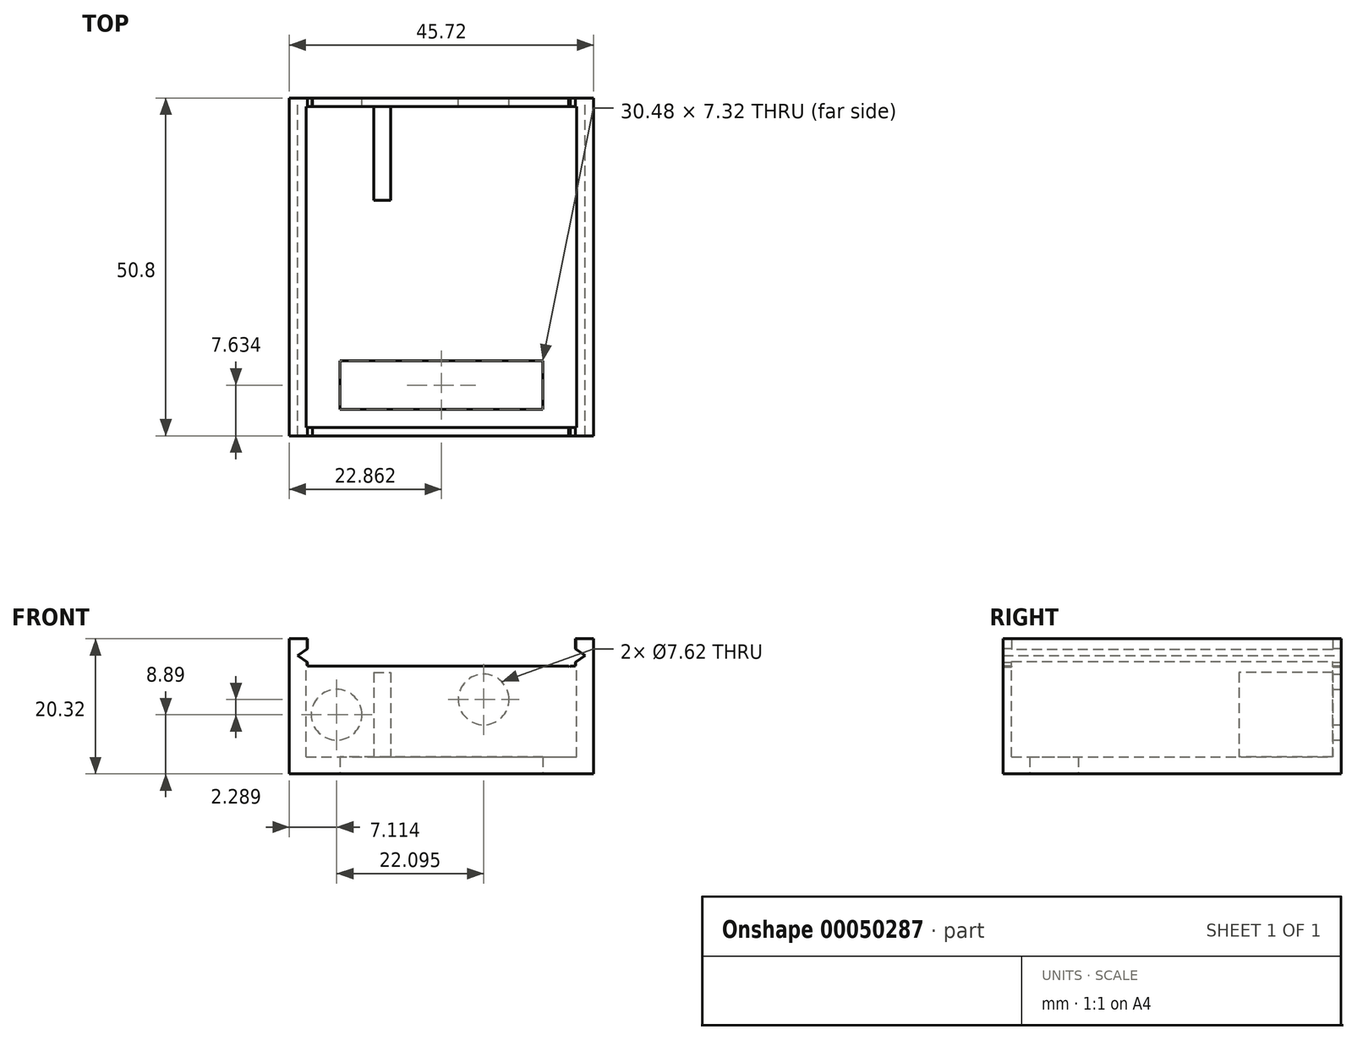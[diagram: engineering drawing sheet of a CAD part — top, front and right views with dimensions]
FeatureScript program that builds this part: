
annotation { "Feature Type Name" : "Feature", "Feature Type Description" : "" }
export const myFeature = defineFeature(function(context is Context, id is Id, definition is map)
    precondition{}
    {
        {
            var Q0;
            Q0=qCreatedBy(makeId("Top.planeOp"),FACE);
            var sketch = newSketch(context, id + "F0", { "sketchPlane" : qUnion([Q0])});
            skLineSegment(sketch, "E0.bottom", {"start": v(-22.55, -23.32) * mm, "end": v(23.17, -23.32) * mm});
            skLineSegment(sketch, "E0.top", {"start": v(-22.55, 27.48) * mm, "end": v(23.17, 27.48) * mm});
            skLineSegment(sketch, "E0.left", {"start": v(-22.55, -23.32) * mm, "end": v(-22.55, 27.48) * mm});
            skLineSegment(sketch, "E0.right", {"start": v(23.17, -23.32) * mm, "end": v(23.17, 27.48) * mm});
            skSolve(sketch);
        }
        {
            var Q0;
            Q0=makeQuery(id+"F0.imprint","IMPRINT",FACE,{"disambiguationData":[TD([[makeQuery(id+"F0.imprint","IMPRINT",EDGE,{"derivedFrom":sQuery(id+"F0.wireOp",EDGE,"E0.bottom")}),1.0]])]});
            extrude(context, id + "F1", {"entities" : qUnion([Q0]), "depth" : 20.32 * mm});
        }
        {
            var Q0;
            Q0=makeQuery(id+"F1.opExtrude","CAP_FACE",FACE,{"disambiguationData":[OSD([sQuery(id+"F0.wireOp",EDGE,"E0.bottom"),sQuery(id+"F0.wireOp",EDGE,"E0.top"),sQuery(id+"F0.wireOp",EDGE,"E0.left"),sQuery(id+"F0.wireOp",EDGE,"E0.right")])],"isStart":true});
            var sketch = newSketch(context, id + "F2", { "sketchPlane" : qUnion([Q0])});
            skLineSegment(sketch, "E1.bottom", {"start": v(-20, 22.05) * mm, "end": v(20.63, 22.05) * mm});
            skLineSegment(sketch, "E1.top", {"start": v(-20, -26.21) * mm, "end": v(20.63, -26.21) * mm});
            skLineSegment(sketch, "E1.left", {"start": v(-20, 22.05) * mm, "end": v(-20, -26.21) * mm});
            skLineSegment(sketch, "E1.right", {"start": v(20.63, 22.05) * mm, "end": v(20.63, -26.21) * mm});
            skSolve(sketch);
        }
        {
            var Q0;
            Q0=makeQuery(id+"F2.imprint","IMPRINT",FACE,{"disambiguationData":[TD([[makeQuery(id+"F2.imprint","IMPRINT",EDGE,{"derivedFrom":sQuery(id+"F2.wireOp",EDGE,"E1.bottom")}),-1.0]])]});
            extrude(context, id + "F3", {"entities" : qUnion([Q0]), "operationType" : NewBodyOperationType.REMOVE, "oppositeDirection" : true, "depth" : 17.78 * mm});
        }
        {
            var Q0;
            Q0=makeQuery(id+"F1.opExtrude","SWEPT_FACE",FACE,{"disambiguationData":[OSD([sQuery(id+"F0.wireOp",EDGE,"E0.top")])]});
            var sketch = newSketch(context, id + "F4", { "sketchPlane" : qUnion([Q0])});
            skSolve(sketch);
        }
        {
            var Q0;
            {var subQ0=sQuery(id+"F0.wireOp",EDGE,"E0.top");Q0=makeQuery(id+"F4.imprint","IMPRINT",FACE,{"disambiguationData":[TD([[makeQuery(id+"F4.imprint","IMPRINT",EDGE,{"derivedFrom":makeQuery(id+"F1.opExtrude","CAP_EDGE",EDGE,{"disambiguationData":[OSD([subQ0])],"isStart":true})}),-1.0]])]});}
            var sketch = newSketch(context, id + "F5", { "sketchPlane" : qUnion([Q0])});
            skLineSegment(sketch, "E2", {"start": v(21.28, 2.54) * mm, "end": v(19.05, 4.1) * mm});
            skLineSegment(sketch, "E3", {"start": v(19.05, 4.1) * mm, "end": v(7.46, -7.14) * mm});
            skLineSegment(sketch, "E4", {"start": v(7.46, -7.14) * mm, "end": v(21.28, 2.54) * mm});
            skLineSegment(sketch, "E5", {"start": v(-19.51, 4.21) * mm, "end": v(-21.9, 2.54) * mm});
            skLineSegment(sketch, "E6", {"start": v(-21.9, 2.54) * mm, "end": v(-16.48, -1.26) * mm});
            skLineSegment(sketch, "E7", {"start": v(-16.48, -1.26) * mm, "end": v(-19.51, 4.21) * mm});
            skSolve(sketch);
        }
        {
            var Q0;
            Q0 = qSketchRegion(id + "F5", true);
            extrude(context, id + "F6", {"entities" : qUnion([Q0]), "operationType" : NewBodyOperationType.REMOVE, "oppositeDirection" : true, "depth" : 76.2 * mm});
        }
        {
            var Q0;
            {var subQ0=sQuery(id+"F0.wireOp",EDGE,"E0.top");Q0=makeQuery(id+"F4.imprint","IMPRINT",FACE,{"disambiguationData":[TD([[makeQuery(id+"F4.imprint","IMPRINT",EDGE,{"derivedFrom":makeQuery(id+"F1.opExtrude","CAP_EDGE",EDGE,{"disambiguationData":[OSD([subQ0])],"isStart":true})}),-1.0]])]});}
            var sketch = newSketch(context, id + "F7", { "sketchPlane" : qUnion([Q0])});
            skLineSegment(sketch, "E8.bottom", {"start": v(-20.43, 4.09) * mm, "end": v(19.8, 4.09) * mm});
            skLineSegment(sketch, "E8.top", {"start": v(-20.43, -9.33) * mm, "end": v(19.8, -9.33) * mm});
            skLineSegment(sketch, "E8.left", {"start": v(-20.43, 4.09) * mm, "end": v(-20.43, -9.33) * mm});
            skLineSegment(sketch, "E8.right", {"start": v(19.8, 4.09) * mm, "end": v(19.8, -9.33) * mm});
            skSolve(sketch);
        }
        {
            var Q0;
            Q0 = qSketchRegion(id + "F7", true);
            extrude(context, id + "F8", {"entities" : qUnion([Q0]), "operationType" : NewBodyOperationType.REMOVE, "oppositeDirection" : true, "depth" : 76.2 * mm});
        }
        {
            var Q0;
            {var subQ0=sQuery(id+"F0.wireOp",EDGE,"E0.top");Q0=makeQuery(id+"F4.imprint","IMPRINT",FACE,{"disambiguationData":[TD([[makeQuery(id+"F4.imprint","IMPRINT",EDGE,{"derivedFrom":makeQuery(id+"F1.opExtrude","CAP_EDGE",EDGE,{"disambiguationData":[OSD([subQ0])],"isStart":true})}),-1.0]])]});}
            var sketch = newSketch(context, id + "F9", { "sketchPlane" : qUnion([Q0])});
            skCircle(sketch, "E9", {"center": v(-6.66, 9.14) * mm, "radius": 3.8 * mm});
            skSolve(sketch);
        }
        {
            var Q0;
            Q0=makeQuery(id+"F9.imprint","IMPRINT",FACE,{"disambiguationData":[TD([[makeQuery(id+"F9.imprint","IMPRINT",EDGE,{"derivedFrom":sQuery(id+"F9.wireOp",EDGE,"E9")}),1.0]])]});
            extrude(context, id + "F10", {"entities" : qUnion([Q0]), "operationType" : NewBodyOperationType.REMOVE, "oppositeDirection" : true, "depth" : 25.4 * mm});
        }
        {
            var Q0;
            {var subQ0=sQuery(id+"F0.wireOp",EDGE,"E0.top");Q0=makeQuery(id+"F4.imprint","IMPRINT",FACE,{"disambiguationData":[TD([[makeQuery(id+"F4.imprint","IMPRINT",EDGE,{"derivedFrom":makeQuery(id+"F1.opExtrude","CAP_EDGE",EDGE,{"disambiguationData":[OSD([subQ0])],"isStart":true})}),-1.0]])]});}
            var sketch = newSketch(context, id + "F11", { "sketchPlane" : qUnion([Q0])});
            skCircle(sketch, "E10", {"center": v(15.44, 11.43) * mm, "radius": 3.81 * mm});
            skSolve(sketch);
        }
        {
            var Q0;
            Q0=makeQuery(id+"F11.imprint","IMPRINT",FACE,{"disambiguationData":[TD([[makeQuery(id+"F11.imprint","IMPRINT",EDGE,{"derivedFrom":sQuery(id+"F11.wireOp",EDGE,"E10")}),1.0]])]});
            extrude(context, id + "F12", {"entities" : qUnion([Q0]), "operationType" : NewBodyOperationType.REMOVE, "oppositeDirection" : true, "depth" : 25.4 * mm});
        }
        {
            var Q0;
            Q0=makeQuery(id+"F1.opExtrude","CAP_FACE",FACE,{"disambiguationData":[OSD([sQuery(id+"F0.wireOp",EDGE,"E0.bottom"),sQuery(id+"F0.wireOp",EDGE,"E0.top"),sQuery(id+"F0.wireOp",EDGE,"E0.left"),sQuery(id+"F0.wireOp",EDGE,"E0.right")])],"isStart":false});
            var sketch = newSketch(context, id + "F13", { "sketchPlane" : qUnion([Q0])});
            skLineSegment(sketch, "E11.bottom", {"start": v(-14.93, -12.03) * mm, "end": v(15.55, -12.03) * mm});
            skLineSegment(sketch, "E11.top", {"start": v(-14.93, -19.34) * mm, "end": v(15.55, -19.34) * mm});
            skLineSegment(sketch, "E11.left", {"start": v(-14.93, -12.03) * mm, "end": v(-14.93, -19.34) * mm});
            skLineSegment(sketch, "E11.right", {"start": v(15.55, -12.03) * mm, "end": v(15.55, -19.34) * mm});
            skSolve(sketch);
        }
        {
            var Q0;
            Q0=makeQuery(id+"F13.imprint","IMPRINT",FACE,{"disambiguationData":[TD([[makeQuery(id+"F13.imprint","IMPRINT",EDGE,{"derivedFrom":sQuery(id+"F13.wireOp",EDGE,"E11.bottom")}),-1.0]])]});
            extrude(context, id + "F14", {"entities" : qUnion([Q0]), "operationType" : NewBodyOperationType.REMOVE, "oppositeDirection" : true, "depth" : 25.4 * mm});
        }
        {
            var Q0;
            Q0=makeQuery(id+"F1.opExtrude","SWEPT_BODY",BODY,{"disambiguationData":[OSD([sQuery(id+"F0.wireOp",EDGE,"E0.bottom"),sQuery(id+"F0.wireOp",EDGE,"E0.top"),sQuery(id+"F0.wireOp",EDGE,"E0.left"),sQuery(id+"F0.wireOp",EDGE,"E0.right")])]});
            var Q1;
            Q1=qCreatedBy(makeId("Top.planeOp"),FACE);
            mirror(context, id + "F15", {"operationType" : NewBodyOperationType.ADD, "entities" : qUnion([Q0]), "mirrorPlane" : qUnion([Q1])});
        }
        {
            var Q0;
            Q0=qCreatedBy(makeId("Front.planeOp"),FACE);
            var sketch = newSketch(context, id + "F16", { "sketchPlane" : qUnion([Q0])});
            skLineSegment(sketch, "E12.bottom", {"start": v(-52.25, 36.5) * mm, "end": v(33.23, 36.5) * mm});
            skLineSegment(sketch, "E12.top", {"start": v(-52.25, 0) * mm, "end": v(33.23, 0) * mm});
            skLineSegment(sketch, "E12.left", {"start": v(-52.25, 36.5) * mm, "end": v(-52.25, 0) * mm});
            skLineSegment(sketch, "E12.right", {"start": v(33.23, 36.5) * mm, "end": v(33.23, 0) * mm});
            skSolve(sketch);
        }
        {
            var Q0;
            Q0=makeQuery(id+"F16.imprint","IMPRINT",FACE,{"disambiguationData":[TD([[makeQuery(id+"F16.imprint","IMPRINT",EDGE,{"derivedFrom":sQuery(id+"F16.wireOp",EDGE,"E12.bottom")}),-1.0]])]});
            extrude(context, id + "F17", {"entities" : qUnion([Q0]), "operationType" : NewBodyOperationType.REMOVE, "endBound" : BoundingType.THROUGH_ALL, "oppositeDirection" : true, "depth" : 25.4 * mm});
        }
        {
            var Q0;
            {var subQ0=sQuery(id+"F0.wireOp",EDGE,"E0.top");Q0=makeQuery(id+"F4.imprint","IMPRINT",FACE,{"disambiguationData":[TD([[makeQuery(id+"F4.imprint","IMPRINT",EDGE,{"derivedFrom":makeQuery(id+"F1.opExtrude","CAP_EDGE",EDGE,{"disambiguationData":[OSD([subQ0])],"isStart":true})}),-1.0]])]});}
            extrude(context, id + "F18", {"entities" : qUnion([Q0]), "operationType" : NewBodyOperationType.REMOVE, "oppositeDirection" : true, "depth" : 1295.4 * mm});
        }
        {
            var Q0;
            Q0=makeQuery(id+"F15.opPattern","COPY",FACE,{"derivedFrom":makeQuery(id+"F3.boolean.opBoolean","COPY",FACE,{"derivedFrom":makeQuery(id+"F3.opExtrude","CAP_FACE",FACE,{"disambiguationData":[OSD([sQuery(id+"F2.wireOp",EDGE,"E1.bottom"),sQuery(id+"F2.wireOp",EDGE,"E1.top"),sQuery(id+"F2.wireOp",EDGE,"E1.left"),sQuery(id+"F2.wireOp",EDGE,"E1.right")])],"isStart":false})}),"instanceName":"1"});
            var sketch = newSketch(context, id + "F19", { "sketchPlane" : qUnion([Q0])});
            skLineSegment(sketch, "E13.bottom", {"start": v(-9.85, 26.21) * mm, "end": v(-7.3, 26.21) * mm});
            skLineSegment(sketch, "E13.top", {"start": v(-9.85, 12.13) * mm, "end": v(-7.3, 12.13) * mm});
            skLineSegment(sketch, "E13.left", {"start": v(-9.85, 26.21) * mm, "end": v(-9.85, 12.13) * mm});
            skLineSegment(sketch, "E13.right", {"start": v(-7.3, 26.21) * mm, "end": v(-7.3, 12.13) * mm});
            skSolve(sketch);
        }
        {
            var Q0;
            Q0=makeQuery(id+"F19.imprint","IMPRINT",FACE,{"disambiguationData":[TD([[makeQuery(id+"F19.imprint","IMPRINT",EDGE,{"derivedFrom":sQuery(id+"F19.wireOp",EDGE,"E13.bottom")}),-1.0]])]});
            extrude(context, id + "F20", {"entities" : qUnion([Q0]), "operationType" : NewBodyOperationType.ADD, "depth" : 12.7 * mm});
        }
    });
